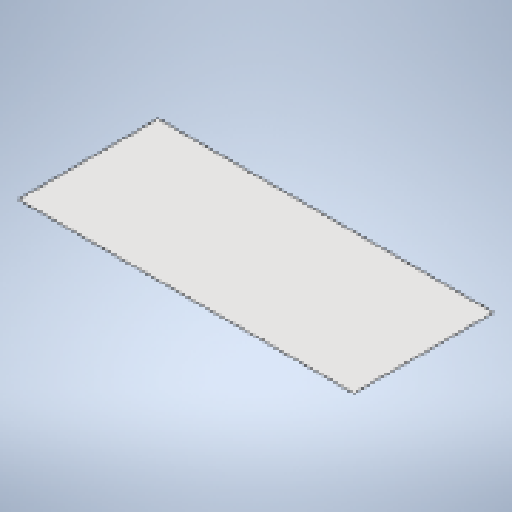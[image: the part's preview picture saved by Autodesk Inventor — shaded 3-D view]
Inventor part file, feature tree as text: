
AUTODESK INVENTOR PART (.ipt)
format: ipt  version: 2025 (Build 290162010, 162A)  size: 135,680 bytes
history: native  units: mm
features: sheet_metal_op x1, sketch x1, other x1
ambient origin geometry x8: Origin, YZ Plane, XZ Plane, XY Plane, X Axis, Y Axis, Z Axis, Center Point
bodies: Solid1 (feature_tree)
feature tree (3):
  sheet_metal_op  "Face1"
  sketch  "Sketch1"  dims[d0=6000.0mm d1=2500.0mm d2=3.0mm]
  other  "Plate1"
